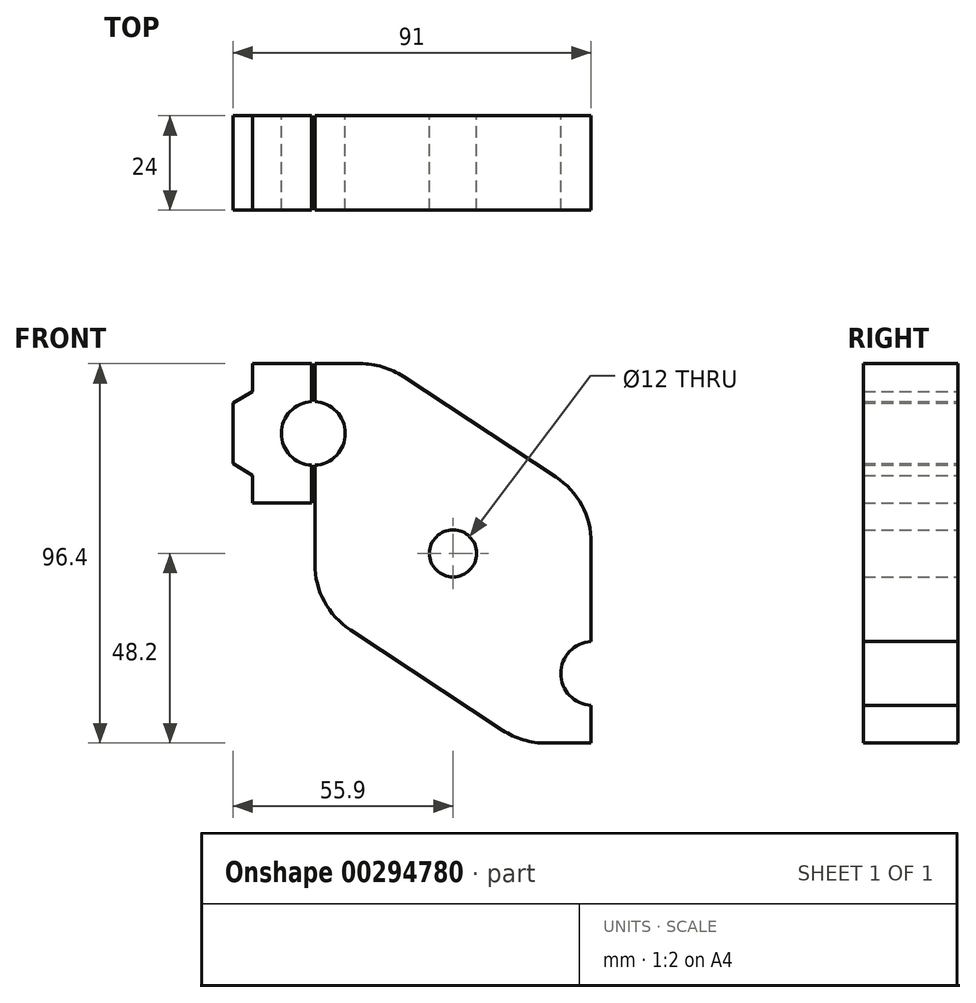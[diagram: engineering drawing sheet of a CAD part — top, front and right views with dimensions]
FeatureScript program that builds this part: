
annotation { "Feature Type Name" : "Feature", "Feature Type Description" : "" }
export const myFeature = defineFeature(function(context is Context, id is Id, definition is map)
    precondition{}
    {
        {
            var Q0;
            Q0=qCreatedBy(makeId("Front.planeOp"),FACE);
            var sketch = newSketch(context, id + "F0", { "sketchPlane" : qUnion([Q0])});
            skLineSegment(sketch, "E0", {"start": v(0, 0) * mm, "end": v(-35.5, 0) * mm, "construction": true});
            skLineSegment(sketch, "E1", {"start": v(-35.5, 0) * mm, "end": v(-35.5, 30.5) * mm, "construction": true});
            skLineSegment(sketch, "E2", {"start": v(0, 0) * mm, "end": v(35.5, 0) * mm, "construction": true});
            skLineSegment(sketch, "E3", {"start": v(35.5, 0) * mm, "end": v(35.5, -30.5) * mm, "construction": true});
            skCircle(sketch, "E4", {"center": v(-35.5, 30.5) * mm, "radius": 7.7 * mm, "construction": true});
            skCircle(sketch, "E5", {"center": v(35.5, -30.5) * mm, "radius": 7.7 * mm, "construction": true});
            skLineSegment(sketch, "E6", {"start": v(-35.5, 30.5) * mm, "end": v(-35.5, 38.2) * mm, "construction": true});
            skLineSegment(sketch, "E7", {"start": v(-35.5, 38.2) * mm, "end": v(-35.5, 48.2) * mm, "construction": true});
            skLineSegment(sketch, "E8", {"start": v(-35.5, 48.2) * mm, "end": v(-35.1, 48.2) * mm, "construction": true});
            skLineSegment(sketch, "E9", {"start": v(-35.5, 48.2) * mm, "end": v(-35.9, 48.2) * mm, "construction": true});
            skLineSegment(sketch, "E10", {"start": v(-35.5, 30.5) * mm, "end": v(-35.5, 22.8) * mm, "construction": true});
            skLineSegment(sketch, "E11", {"start": v(-35.5, 22.8) * mm, "end": v(-35.5, 12.8) * mm, "construction": true});
            skLineSegment(sketch, "E12", {"start": v(-35.5, 12.8) * mm, "end": v(-35.9, 12.8) * mm, "construction": true});
            skLineSegment(sketch, "E13", {"start": v(-35.5, 12.8) * mm, "end": v(-35.1, 12.8) * mm, "construction": true});
            skArc(sketch, "E14", {"start": v(-35.1, 22.4) * mm, "mid": v(-27.4, 30.5) * mm, "end": v(-35.1, 38.6) * mm});
            skLineSegment(sketch, "E15", {"start": v(-35.9, 48.2) * mm, "end": v(-35.9, 38.6) * mm});
            skLineSegment(sketch, "E16", {"start": v(-35.1, 48.2) * mm, "end": v(-35.1, 38.6) * mm});
            skLineSegment(sketch, "E17", {"start": v(-35.9, 12.8) * mm, "end": v(-35.9, 22.4) * mm});
            skLineSegment(sketch, "E18", {"start": v(-35.1, 12.8) * mm, "end": v(-35.1, 22.4) * mm});
            skArc(sketch, "E19.trimOffspring", {"start": v(-35.9, 38.6) * mm, "mid": v(-43.6, 30.5) * mm, "end": v(-35.9, 22.4) * mm});
            skLineSegment(sketch, "E20", {"start": v(-35.9, 12.8) * mm, "end": v(-50.9, 12.8) * mm});
            skLineSegment(sketch, "E21", {"start": v(-35.9, 48.2) * mm, "end": v(-50.9, 48.2) * mm});
            skLineSegment(sketch, "E22", {"start": v(-55.9, 22.8) * mm, "end": v(-55.9, 38.2) * mm});
            skLineSegment(sketch, "E23", {"start": v(-35.9, 22.4) * mm, "end": v(-35.5, 22.4) * mm, "construction": true});
            skLineSegment(sketch, "E24", {"start": v(-35.5, 22.4) * mm, "end": v(-35.1, 22.4) * mm, "construction": true});
            skLineSegment(sketch, "E25", {"start": v(-35.9, 38.6) * mm, "end": v(-35.5, 38.6) * mm, "construction": true});
            skLineSegment(sketch, "E26", {"start": v(-35.5, 38.6) * mm, "end": v(-35.1, 38.6) * mm, "construction": true});
            skLineSegment(sketch, "E27", {"start": v(-50.9, 48.2) * mm, "end": v(-50.9, 41.2) * mm});
            skLineSegment(sketch, "E28", {"start": v(-50.9, 12.8) * mm, "end": v(-50.9, 19.8) * mm});
            skLineSegment(sketch, "E29", {"start": v(-55.9, 38.2) * mm, "end": v(-50.9, 41.2) * mm});
            skLineSegment(sketch, "E30", {"start": v(-55.9, 22.8) * mm, "end": v(-50.9, 19.8) * mm});
            skPoint(sketch, "E31.start.orphan", {"position": v(-55.9, 48.2) * mm});
            skPoint(sketch, "E32.start.orphan", {"position": v(-55.9, 12.8) * mm});
            skCircle(sketch, "E33", {"center": v(35.5, -30.5) * mm, "radius": 8.1 * mm});
            skLineSegment(sketch, "E34", {"start": v(35.5, -30.5) * mm, "end": v(35.5, -38.2) * mm, "construction": true});
            skLineSegment(sketch, "E35", {"start": v(35.5, -38.2) * mm, "end": v(35.5, -48.2) * mm, "construction": true});
            skLineSegment(sketch, "E36", {"start": v(35.5, -48.2) * mm, "end": v(37.73, -48.2) * mm, "construction": true});
            skLineSegment(sketch, "E37", {"start": v(35.5, -48.2) * mm, "end": v(35.1, -48.2) * mm, "construction": true});
            skLineSegment(sketch, "E38", {"start": v(35.5, -22.8) * mm, "end": v(35.5, -12.8) * mm, "construction": true});
            skLineSegment(sketch, "E39", {"start": v(35.5, -12.8) * mm, "end": v(35.1, -12.8) * mm, "construction": true});
            skLineSegment(sketch, "E40", {"start": v(35.5, -12.8) * mm, "end": v(35.9, -12.8) * mm, "construction": true});
            skLineSegment(sketch, "E41", {"start": v(35.1, -48.2) * mm, "end": v(35.1, -38.6) * mm});
            skLineSegment(sketch, "E42", {"start": v(35.1, -12.8) * mm, "end": v(35.1, -22.4) * mm});
            skLineSegment(sketch, "E43", {"start": v(35.1, -48.2) * mm, "end": v(17.6, -48.2) * mm});
            skLineSegment(sketch, "E44", {"start": v(-35.1, 48.2) * mm, "end": v(-17.6, 48.2) * mm});
            skLineSegment(sketch, "E45", {"start": v(-35.1, 12.8) * mm, "end": v(-35.1, -13.5) * mm});
            skLineSegment(sketch, "E46", {"start": v(35.1, -12.8) * mm, "end": v(35.1, 0) * mm});
            skCircle(sketch, "E47", {"center": v(0, 0) * mm, "radius": 6 * mm});
            skLineSegment(sketch, "E48", {"start": v(-35.1, 0) * mm, "end": v(-35.1, -2.72) * mm});
            skLineSegment(sketch, "E49", {"start": v(35.1, -48.2) * mm, "end": v(23.6, -48.2) * mm});
            skLineSegment(sketch, "E50", {"start": v(-26.1, -19.43) * mm, "end": v(12.6, -44.9) * mm});
            skLineSegment(sketch, "E51", {"start": v(35.1, 0) * mm, "end": v(35.1, 2.72) * mm});
            skLineSegment(sketch, "E52", {"start": v(-35.1, 48.2) * mm, "end": v(-23.6, 48.2) * mm});
            skLineSegment(sketch, "E53", {"start": v(26.1, 19.43) * mm, "end": v(-12.6, 44.9) * mm});
            skPoint(sketch, "E54.visualSharp", {"position": v(17.6, -48.2) * mm});
            skArc(sketch, "E54.filletArc", {"start": v(12.6, -44.9) * mm, "mid": v(17.85, -47.36) * mm, "end": v(23.6, -48.2) * mm});
            skPoint(sketch, "E55.visualSharp", {"position": v(-35.1, -13.5) * mm});
            skArc(sketch, "E55.filletArc", {"start": v(-35.1, -2.72) * mm, "mid": v(-32.7, -12.21) * mm, "end": v(-26.1, -19.43) * mm});
            skPoint(sketch, "E56.visualSharp", {"position": v(35.1, 13.5) * mm});
            skArc(sketch, "E56.filletArc", {"start": v(35.1, 2.72) * mm, "mid": v(32.7, 12.21) * mm, "end": v(26.1, 19.43) * mm});
            skPoint(sketch, "E57.visualSharp", {"position": v(-17.6, 48.2) * mm});
            skArc(sketch, "E57.filletArc", {"start": v(-12.6, 44.9) * mm, "mid": v(-17.85, 47.36) * mm, "end": v(-23.6, 48.2) * mm});
            skSolve(sketch);
        }
        {
            var Q0;
            Q0=makeQuery(id+"F0.imprint","IMPRINT",FACE,{"disambiguationData":[TD([[makeQuery(id+"F0.imprint","IMPRINT",EDGE,{"derivedFrom":sQuery(id+"F0.wireOp",EDGE,"E15")}),-1.0]])]});
            extrude(context, id + "F1", {"entities" : qUnion([Q0]), "depth" : 24 * mm});
        }
        {
            var Q0;
            Q0=makeQuery(id+"F0.imprint","IMPRINT",FACE,{"disambiguationData":[TD([[makeQuery(id+"F0.imprint","IMPRINT",EDGE,{"derivedFrom":sQuery(id+"F0.wireOp",EDGE,"E14")}),-1.0]])]});
            extrude(context, id + "F2", {"entities" : qUnion([Q0]), "depth" : 24 * mm});
        }
    });
